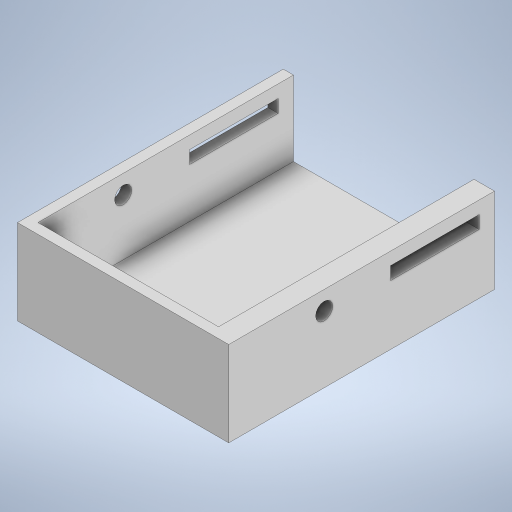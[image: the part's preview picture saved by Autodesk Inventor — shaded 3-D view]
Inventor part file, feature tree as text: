
AUTODESK INVENTOR PART (.ipt)
format: ipt  version: 2023 (Build 270158000, 158)  size: 251,904 bytes
history: native  units: in
note: dims shown in document units (in); Inventor stores cm internally (conversion verified against a paired STEP export)
features: sketch x6, extrude x5, shell x1
ambient origin geometry x8: Origin, YZ Plane, XZ Plane, XY Plane, X Axis, Y Axis, Z Axis, Center Point
bodies: Solid1 (feature_tree)
feature tree (12):
  extrude  "Extrusion1"  Depth=3.0709in
  shell  "Shell1"  Thickness=0.9843in
  sketch  "Sketch4"  dims[d4=0.1181in d17=0.3937in d18=0.0in]
  extrude  "Extrusion3"  Depth=0.3937in TaperAngle=0.0deg
  sketch  "Sketch6"  dims[d21=0.1772in d22=0.689in]
  extrude  "Extrusion5"  Depth=0.1496in
  extrude  "Extrusion6"  Depth=0.689in
  extrude  "Extrusion7"  TaperAngle=0.0deg  [1 undecoded]
  sketch  "Sketch2"  dims[d0=2.3228in d1=3.0709in d2=0.9843in d3=0.0in]
  sketch  "Sketch5"  dims[d19=1.0236in d20=0.1496in]
  sketch  "Sketch7"  dims[d25=0.1181in d26=0.0in d27=0.0in d28=0.0in]
  sketch  "Sketch8"  dims[d29=0.1969in d30=0.0in d31=0.0in d13=0.0197in d14=0.0344in d15=0.0197in d16=0.0344in d32=0.0197in d33=0.0344in]
note: 1 required parameter value undecoded (feature->parameter linkage not recoverable at this tier; creation-order binding heuristic only, values carry confidence <= 0.55)
